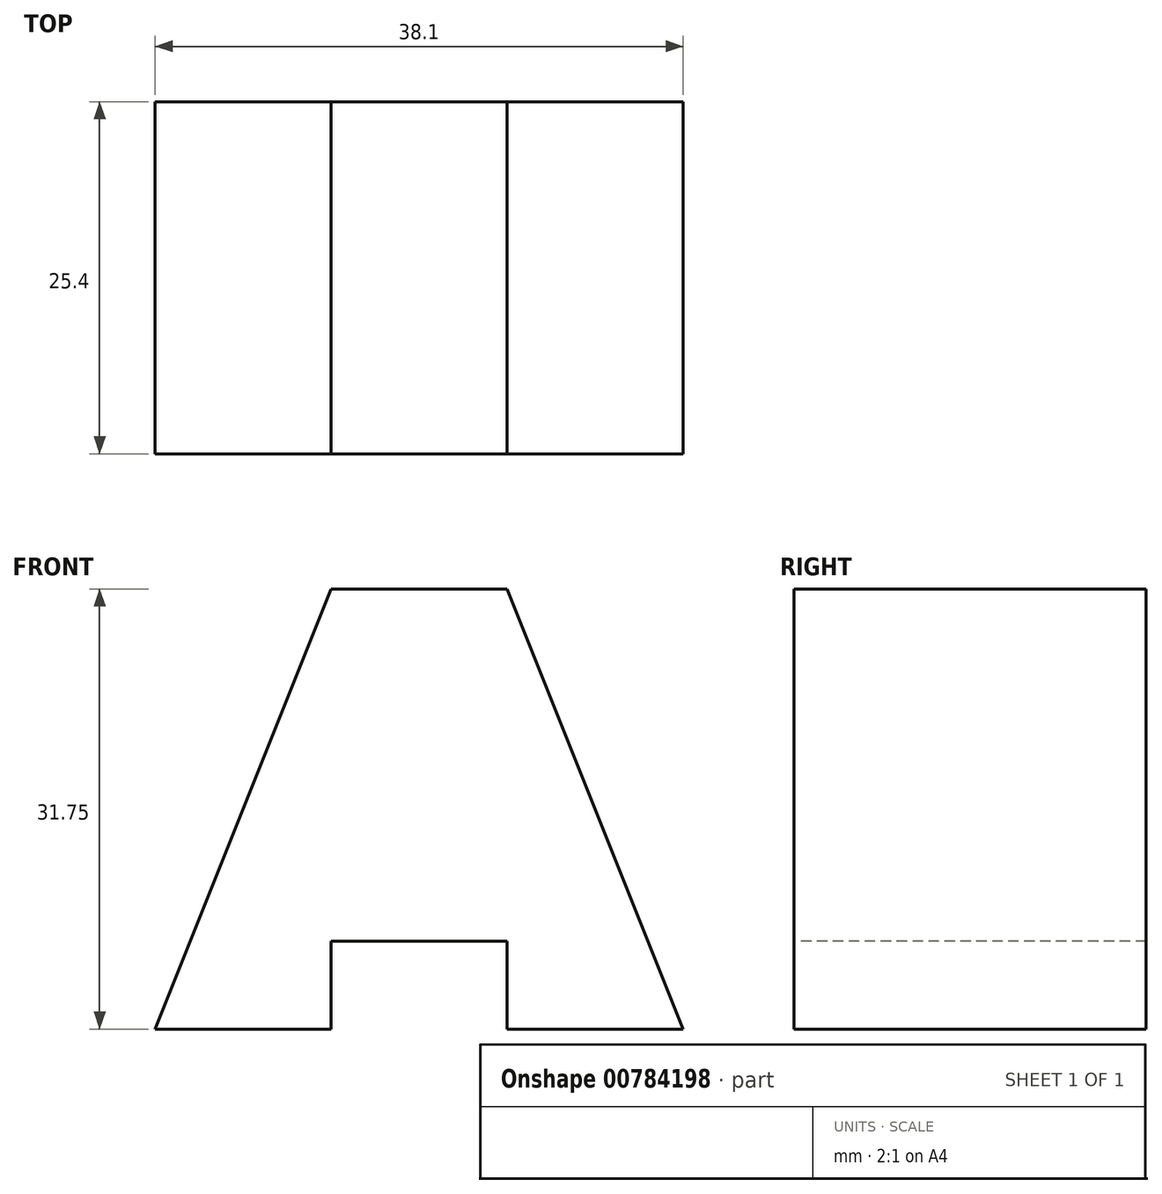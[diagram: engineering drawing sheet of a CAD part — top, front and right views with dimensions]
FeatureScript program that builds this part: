
annotation { "Feature Type Name" : "Feature", "Feature Type Description" : "" }
export const myFeature = defineFeature(function(context is Context, id is Id, definition is map)
    precondition{}
    {
        {
            var Q0;
            Q0=qCreatedBy(makeId("Front.planeOp"),FACE);
            var sketch = newSketch(context, id + "F0", { "sketchPlane" : qUnion([Q0])});
            skLineSegment(sketch, "E0", {"start": v(0, 0) * mm, "end": v(38.1, 0) * mm});
            skLineSegment(sketch, "E1", {"start": v(38.1, 0) * mm, "end": v(38.1, 31.75) * mm});
            skLineSegment(sketch, "E2", {"start": v(38.1, 31.75) * mm, "end": v(0, 31.75) * mm});
            skLineSegment(sketch, "E3", {"start": v(0, 31.75) * mm, "end": v(0, 0) * mm});
            skSolve(sketch);
        }
        {
            var Q0;
            Q0=makeQuery(id+"F0.imprint","IMPRINT",FACE,{"disambiguationData":[TD([[makeQuery(id+"F0.imprint","IMPRINT",EDGE,{"derivedFrom":sQuery(id+"F0.wireOp",EDGE,"E0")}),1.0]])]});
            extrude(context, id + "F1", {"entities" : qUnion([Q0]), "depth" : 25.4 * mm, "offsetDistance" : 25.4 * mm});
        }
        {
            var Q0;
            Q0=makeQuery(id+"F1.opExtrude","CAP_FACE",FACE,{"disambiguationData":[OSD([sQuery(id+"F0.wireOp",EDGE,"E0"),sQuery(id+"F0.wireOp",EDGE,"E1"),sQuery(id+"F0.wireOp",EDGE,"E2"),sQuery(id+"F0.wireOp",EDGE,"E3")])],"isStart":false});
            var sketch = newSketch(context, id + "F2", { "sketchPlane" : qUnion([Q0])});
            skLineSegment(sketch, "E4", {"start": v(0, 0) * mm, "end": v(12.7, 0) * mm});
            skLineSegment(sketch, "E5", {"start": v(12.7, 0) * mm, "end": v(12.7, 6.35) * mm});
            skLineSegment(sketch, "E6", {"start": v(12.7, 6.35) * mm, "end": v(25.4, 6.35) * mm});
            skLineSegment(sketch, "E7", {"start": v(25.4, 6.35) * mm, "end": v(25.4, 0) * mm});
            skLineSegment(sketch, "E8", {"start": v(25.4, 0) * mm, "end": v(38.1, 0) * mm});
            skLineSegment(sketch, "E9", {"start": v(38.1, 0) * mm, "end": v(25.4, 31.75) * mm});
            skLineSegment(sketch, "E10", {"start": v(25.4, 31.75) * mm, "end": v(12.7, 31.75) * mm});
            skLineSegment(sketch, "E11", {"start": v(12.7, 31.75) * mm, "end": v(0, 0) * mm});
            skSolve(sketch);
        }
        {
            var Q0;
            {var subQ0=sQuery(id+"F2.wireOp",EDGE,"E5");Q0=makeQuery(id+"F2.imprint","IMPRINT",FACE,{"disambiguationData":[TD([[makeQuery(id+"F2.imprint","IMPRINT",EDGE,{"derivedFrom":subQ0}),-1.0]])]});}
            extrude(context, id + "F3", {"entities" : qUnion([Q0]), "operationType" : NewBodyOperationType.REMOVE, "oppositeDirection" : true, "depth" : 25.4 * mm, "offsetDistance" : 25.4 * mm});
        }
        {
            var Q0;
            Q0=makeQuery(id+"F1.opExtrude","CAP_FACE",FACE,{"disambiguationData":[OSD([sQuery(id+"F0.wireOp",EDGE,"E0"),sQuery(id+"F0.wireOp",EDGE,"E1"),sQuery(id+"F0.wireOp",EDGE,"E2"),sQuery(id+"F0.wireOp",EDGE,"E3")])],"isStart":false});
            var sketch = newSketch(context, id + "F4", { "sketchPlane" : qUnion([Q0])});
            skLineSegment(sketch, "E12", {"start": v(0, 0) * mm, "end": v(12.7, 31.75) * mm});
            skLineSegment(sketch, "E13", {"start": v(12.7, 31.75) * mm, "end": v(0, 31.75) * mm});
            skLineSegment(sketch, "E14", {"start": v(0, 31.75) * mm, "end": v(0, 0) * mm});
            skSolve(sketch);
        }
        {
            var Q0;
            Q0=makeQuery(id+"F4.imprint","IMPRINT",FACE,{"disambiguationData":[TD([[makeQuery(id+"F4.imprint","IMPRINT",EDGE,{"derivedFrom":sQuery(id+"F4.wireOp",EDGE,"E12")}),1.0]])]});
            extrude(context, id + "F5", {"entities" : qUnion([Q0]), "operationType" : NewBodyOperationType.REMOVE, "oppositeDirection" : true, "depth" : 25.4 * mm, "offsetDistance" : 25.4 * mm});
        }
        {
            var Q0;
            Q0=makeQuery(id+"F1.opExtrude","CAP_FACE",FACE,{"disambiguationData":[OSD([sQuery(id+"F0.wireOp",EDGE,"E0"),sQuery(id+"F0.wireOp",EDGE,"E1"),sQuery(id+"F0.wireOp",EDGE,"E2"),sQuery(id+"F0.wireOp",EDGE,"E3")])],"isStart":false});
            var sketch = newSketch(context, id + "F6", { "sketchPlane" : qUnion([Q0])});
            skLineSegment(sketch, "E15", {"start": v(38.1, 0) * mm, "end": v(25.4, 31.75) * mm});
            skLineSegment(sketch, "E16", {"start": v(25.4, 31.75) * mm, "end": v(38.1, 31.75) * mm});
            skLineSegment(sketch, "E17", {"start": v(38.1, 31.75) * mm, "end": v(38.1, 0) * mm});
            skSolve(sketch);
        }
        {
            var Q0;
            Q0=makeQuery(id+"F6.imprint","IMPRINT",FACE,{"disambiguationData":[TD([[makeQuery(id+"F6.imprint","IMPRINT",EDGE,{"derivedFrom":sQuery(id+"F6.wireOp",EDGE,"E15")}),-1.0]])]});
            extrude(context, id + "F7", {"entities" : qUnion([Q0]), "operationType" : NewBodyOperationType.REMOVE, "oppositeDirection" : true, "depth" : 25.4 * mm, "offsetDistance" : 25.4 * mm});
        }
    });
